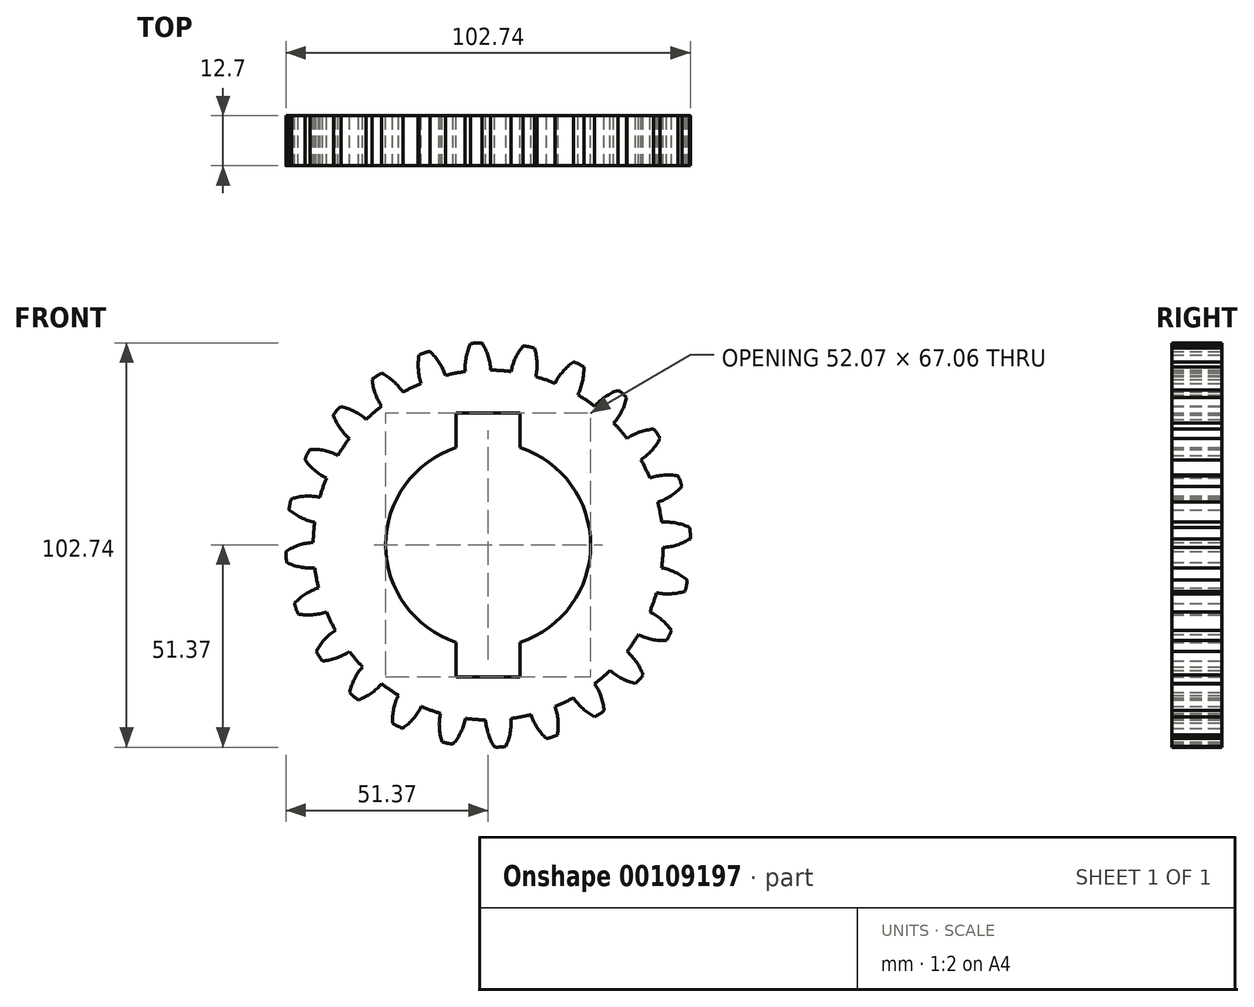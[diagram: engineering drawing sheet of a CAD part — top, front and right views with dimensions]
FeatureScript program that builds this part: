
annotation { "Feature Type Name" : "Feature", "Feature Type Description" : "" }
export const myFeature = defineFeature(function(context is Context, id is Id, definition is map)
    precondition{}
    {
        {
            var Q0;
            Q0=qCreatedBy(makeId("Front.planeOp"),FACE);
            var sketch = newSketch(context, id + "F0", { "sketchPlane" : qUnion([Q0])});
            skCircle(sketch, "E0", {"center": v(0, 0) * mm, "radius": 26.04 * mm});
            skCircle(sketch, "E1", {"center": v(0, 0) * mm, "radius": 44.45 * mm});
            skLineSegment(sketch, "E2", {"start": v(0, 56.3) * mm, "end": v(0, -55.83) * mm, "construction": true});
            skCircle(sketch, "E3", {"center": v(0.32, 0) * mm, "radius": 51.37 * mm, "construction": true});
            skCircle(sketch, "E4", {"center": v(0.32, 0) * mm, "radius": 47.93 * mm, "construction": true});
            skCircle(sketch, "E5", {"center": v(0.32, 0) * mm, "radius": 45.8 * mm, "construction": true});
            skLineSegment(sketch, "E6", {"start": v(0.32, 0) * mm, "end": v(-3.35, 56.06) * mm, "construction": true});
            skCircle(sketch, "E7", {"center": v(0, 47.93) * mm, "radius": 14.6 * mm, "construction": true});
            skCircle(sketch, "E8", {"center": v(-13.93, 43.53) * mm, "radius": 14.6 * mm, "construction": true});
            skArc(sketch, "E9", {"start": v(0.65, 44.45) * mm, "mid": v(-0.03, 48.03) * mm, "end": v(-1.59, 51.34) * mm});
            skArc(sketch, "E10.MirrorCS", {"start": v(-5.8, 44.02) * mm, "mid": v(-5.6, 47.67) * mm, "end": v(-4.5, 51.15) * mm});
            skArc(sketch, "E11", {"start": v(-1.59, 51.34) * mm, "mid": v(-3.05, 51.35) * mm, "end": v(-4.5, 51.15) * mm});
            skLineSegment(sketch, "E12.bottom", {"start": v(-8.13, -33.53) * mm, "end": v(8.13, -33.53) * mm});
            skLineSegment(sketch, "E12.top", {"start": v(-8.13, 33.53) * mm, "end": v(8.13, 33.53) * mm});
            skLineSegment(sketch, "E12.left", {"start": v(-8.13, -33.53) * mm, "end": v(-8.13, 33.53) * mm});
            skLineSegment(sketch, "E12.right", {"start": v(8.13, -33.53) * mm, "end": v(8.13, 33.53) * mm});
            skSolve(sketch);
        }
        {
            var Q0;
            Q0=qSketchRegion(id+"F0",true);
            extrude(context, id + "F1", {"entities" : qUnion([Q0]), "depth" : 12.7 * mm});
        }
        {
            var Q0;
            Q0=makeQuery(id+"F1.opExtrude","SWEPT_BODY",BODY,{"disambiguationData":[OSD([sQuery(id+"F0.wireOp",EDGE,"E1"),sQuery(id+"F0.wireOp",EDGE,"E9"),sQuery(id+"F0.wireOp",EDGE,"E10.MirrorCS"),sQuery(id+"F0.wireOp",EDGE,"E11"),sQuery(id+"F0.wireOp",EDGE,"mQY0wwNy-6cYu-q0qe-OCgn-TzdDa7zRngHh"),sQuery(id+"F0.wireOp",EDGE,"E12.bottom"),sQuery(id+"F0.wireOp",EDGE,"E12.top"),sQuery(id+"F0.wireOp",EDGE,"E12.left"),sQuery(id+"F0.wireOp",EDGE,"E12.right")])]});
            var Q1;
            Q1=makeQuery(id+"F1.opExtrude","SWEPT_FACE",FACE,{"disambiguationData":[OSD([sQuery(id+"F0.wireOp",EDGE,"E1")])]});
            circularPattern(context, id + "F2", {"operationType" : NewBodyOperationType.ADD, "entities" : qUnion([Q0]), "axis" : qUnion([Q1]), "angle" : 15 * degree, "instanceCount" : 24});
        }
        {
            var Q0;
            {var subQ5=sQuery(id+"F0.wireOp",EDGE,"E12.top");Q0=makeQuery(id+"F0.imprint","IMPRINT",FACE,{"disambiguationData":[TD([[makeQuery(id+"F0.imprint","IMPRINT",EDGE,{"derivedFrom":subQ5}),-1.0]])]});}
            var Q1;
            {var subQ0=sQuery(id+"F0.wireOp",EDGE,"E12.left");var subQ1=sQuery(id+"F0.wireOp",EDGE,"mQY0wwNy-6cYu-q0qe-OCgn-TzdDa7zRngHh");var subQ2=makeQuery(id+"F0.imprint","INTERSECT",VERTEX,{"disambiguationData":[OD(0.0)],"derivedFrom":[subQ1,subQ0]});Q1=makeQuery(id+"F0.imprint","IMPRINT",FACE,{"disambiguationData":[TD([[makeQuery(id+"F0.imprint","IMPRINT",EDGE,{"disambiguationData":[TD([[subQ2,1.0]])],"derivedFrom":subQ1}),1.0]])]});}
            var Q2;
            {var subQ5=sQuery(id+"F0.wireOp",EDGE,"E12.bottom");Q2=makeQuery(id+"F0.imprint","IMPRINT",FACE,{"disambiguationData":[TD([[makeQuery(id+"F0.imprint","IMPRINT",EDGE,{"derivedFrom":subQ5}),1.0]])]});}
            extrude(context, id + "F3", {"entities" : qUnion([Q0, Q1, Q2]), "endBound" : BoundingType.SYMMETRIC, "depth" : 50.8 * mm});
        }
        {
            var Q0;
            Q0=makeQuery(id+"F3.opExtrude","SWEPT_BODY",BODY,{"disambiguationData":[OSD([sQuery(id+"F0.wireOp",EDGE,"E12.bottom"),sQuery(id+"F0.wireOp",EDGE,"E12.top"),sQuery(id+"F0.wireOp",EDGE,"E12.left"),sQuery(id+"F0.wireOp",EDGE,"E12.right")])]});
            var Q1;
            Q1=makeQuery(id+"F1.opExtrude","SWEPT_BODY",BODY,{"disambiguationData":[OSD([sQuery(id+"F0.wireOp",EDGE,"E1"),sQuery(id+"F0.wireOp",EDGE,"E9"),sQuery(id+"F0.wireOp",EDGE,"E10.MirrorCS"),sQuery(id+"F0.wireOp",EDGE,"E11"),sQuery(id+"F0.wireOp",EDGE,"mQY0wwNy-6cYu-q0qe-OCgn-TzdDa7zRngHh"),sQuery(id+"F0.wireOp",EDGE,"E12.bottom"),sQuery(id+"F0.wireOp",EDGE,"E12.top"),sQuery(id+"F0.wireOp",EDGE,"E12.left"),sQuery(id+"F0.wireOp",EDGE,"E12.right")])]});
            booleanBodies(context, id + "F4", {"operationType" : BooleanOperationType.SUBTRACTION, "tools" : qUnion([Q0]), "targets" : qUnion([Q1])});
        }
    });
